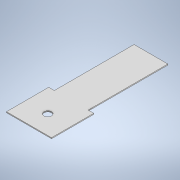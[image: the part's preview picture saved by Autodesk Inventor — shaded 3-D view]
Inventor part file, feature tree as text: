
AUTODESK INVENTOR PART (.ipt)
format: ipt  version: 2022.3 (Build 263350000, 350)  size: 104,448 bytes
history: native  units: in
note: dims shown in document units (in); Inventor stores cm internally (conversion verified against a paired STEP export)
features: extrude x1, sketch x1
ambient origin geometry x8: Origin, YZ Plane, XZ Plane, XY Plane, X Axis, Y Axis, Z Axis, Center Point
bodies: Solid1 (feature_tree)
feature tree (2):
  extrude  "Extrusion1"  Depth=1.7717in
  sketch  "Sketch1"  dims[d0=1.8898in d1=1.7717in d2=1.4173in d3=3.3465in d6=0.6299in d7=0.2362in d8=0.315in d9=0.0394in d10=0.0in]
